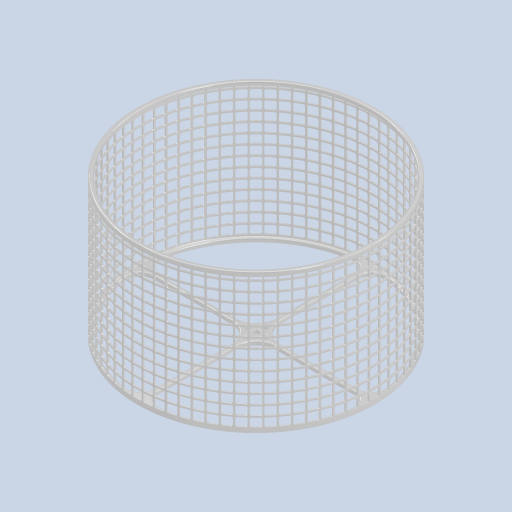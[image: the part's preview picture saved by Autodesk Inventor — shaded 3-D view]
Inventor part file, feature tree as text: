
AUTODESK INVENTOR PART (.ipt)
format: ipt  version: 2023 (Build 270158000, 158)  size: 15,778,816 bytes
history: native  units: mm
features: extrude x5, fillet x3, sketch x3, pattern_circular x2, pattern_linear x1
ambient origin geometry x8: Origin, YZ Plane, XZ Plane, XY Plane, X Axis, Y Axis, Z Axis, Center Point
bodies: Solid1 (feature_tree)
feature tree (14):
  extrude  "Extrusion1"  Depth=3.0mm
  fillet  "Fillet1"  Radius=3.0mm
  sketch  "Sketch2"  dims[d3=1.5mm d4=85.0mm]
  extrude  "Extrusion5"  Depth=85.0mm
  extrude  "Extrusion2"  Depth=1.0mm TaperAngle=360.0deg
  extrude  "Extrusion3"  Depth=1.0mm TaperAngle=0.0deg
  pattern_linear  "Rectangular Pattern1"  Spacing1=0.872665mm  [1 undecoded]
  extrude  "Extrusion4"  Depth=1.0mm
  pattern_circular  "Circular Pattern3"  [2 undecoded]
  fillet  "Fillet3"  Radius=0.872665mm
  fillet  "Fillet7"  Radius=84.0mm
  pattern_circular  "Circular Pattern2"  [2 undecoded]
  sketch  "Sketch1"  dims[d0=170.0mm d1=3.0mm d2=3.0mm]
  sketch  "Sketch4"  dims[d5=0.0mm d6=40.0mm d8=360.0deg d10=3.0mm d11=0.0mm d20=0.872665mm d21=85.0mm d22=0.436332mm d23=0.872665mm d24=84.0mm d25=0.436332mm d26=0.5mm d27=94.0mm d28=0.0mm d29=1.0mm d30=0.0mm d31=140.0mm d33=7.0mm d37=164.0mm d38=3.0mm d39=0.0mm d40=1.0mm d45=4.2mm d48=12.7mm d49=3.4mm d55=10.0mm d56=15.0mm d57=10.0mm d58=0.0mm d62=720.0mm d63=360.0deg d69=40.0mm d70=360.0deg d73=1.0mm d74=0.5mm d13=0.0mm d14=0.0mm d15=0.0mm d16=0.0mm d32=0.872665mm d76=0.0mm d77=0.0mm d78=0.0mm]
note: 5 required parameter values undecoded (feature->parameter linkage not recoverable at this tier; creation-order binding heuristic only, values carry confidence <= 0.55)
